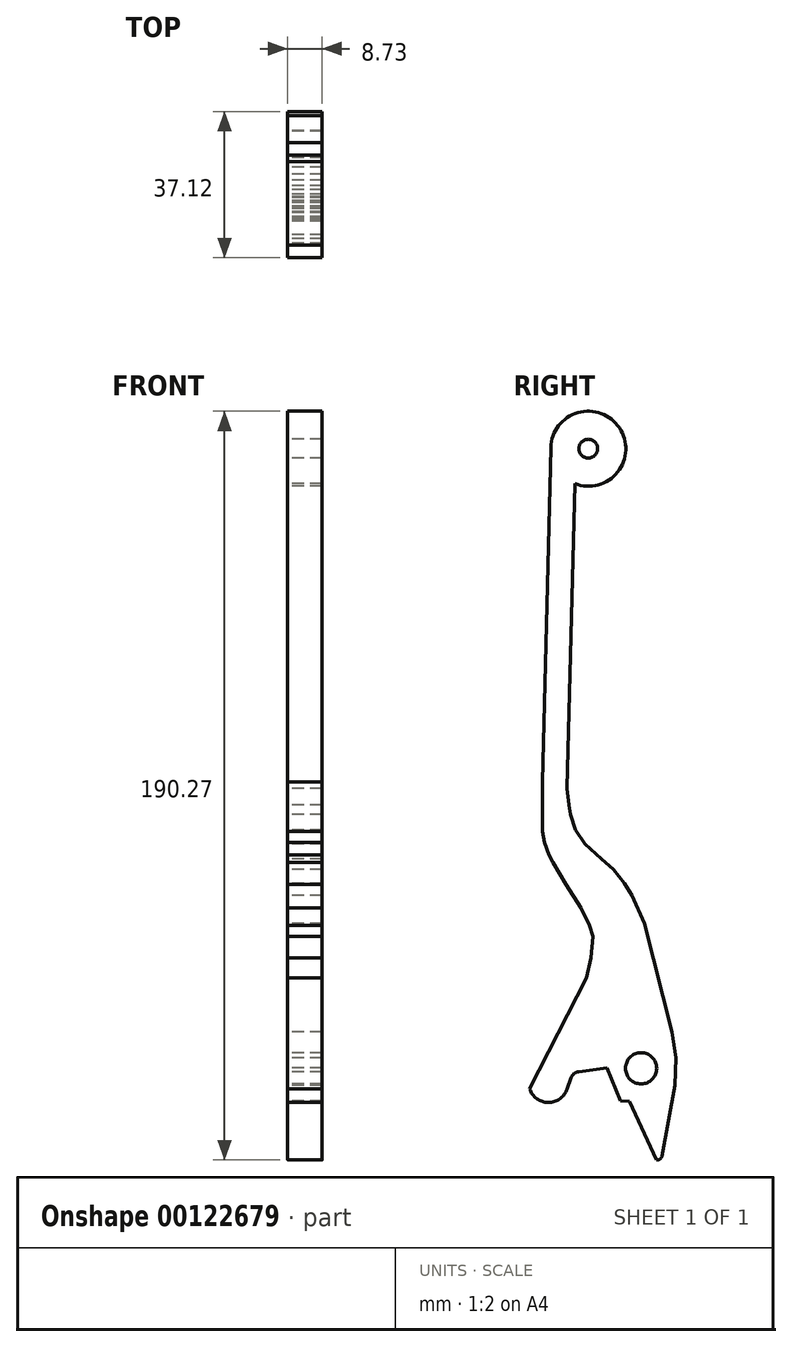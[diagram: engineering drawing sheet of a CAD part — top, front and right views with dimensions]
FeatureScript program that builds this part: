
annotation { "Feature Type Name" : "Feature", "Feature Type Description" : "" }
export const myFeature = defineFeature(function(context is Context, id is Id, definition is map)
    precondition{}
    {
        {
            var Q0;
            Q0=qCreatedBy(makeId("Right.planeOp"),FACE);
            var sketch = newSketch(context, id + "F0", { "sketchPlane" : qUnion([Q0])});
            skLineSegment(sketch, "E0", {"start": v(18.14, 76.71) * mm, "end": v(13.92, -75.63) * mm});
            skLineSegment(sketch, "E1", {"start": v(-35.24, -55.96) * mm, "end": v(-22.74, -31.58) * mm});
            skLineSegment(sketch, "E2", {"start": v(-22.7, -51.6) * mm, "end": v(-15.56, -50.57) * mm});
            skLineSegment(sketch, "E3", {"start": v(-12.21, -58.94) * mm, "end": v(-9.84, -59.08) * mm});
            skLineSegment(sketch, "E4", {"start": v(-9.84, -59.08) * mm, "end": v(-3.05, -74) * mm});
            skLineSegment(sketch, "E5", {"start": v(-1.7, -73.13) * mm, "end": v(1.67, -55.09) * mm});
            skLineSegment(sketch, "E6", {"start": v(1.67, -55.09) * mm, "end": v(1.88, -48.09) * mm});
            skLineSegment(sketch, "E7", {"start": v(1.88, -48.09) * mm, "end": v(0.85, -41.52) * mm});
            skLineSegment(sketch, "E8", {"start": v(0.85, -41.52) * mm, "end": v(-6.04, -13.87) * mm});
            skLineSegment(sketch, "E9", {"start": v(-6.04, -13.87) * mm, "end": v(-9.21, -6.82) * mm});
            skLineSegment(sketch, "E10", {"start": v(-9.21, -6.82) * mm, "end": v(-11.14, -3.78) * mm});
            skLineSegment(sketch, "E11", {"start": v(-11.14, -3.78) * mm, "end": v(-14.02, -0.25) * mm});
            skLineSegment(sketch, "E12", {"start": v(-14.02, -0.25) * mm, "end": v(-16.96, 2.48) * mm});
            skLineSegment(sketch, "E13", {"start": v(-16.96, 2.48) * mm, "end": v(-21.24, 6.3) * mm});
            skLineSegment(sketch, "E14", {"start": v(-21.24, 6.3) * mm, "end": v(-23.6, 9.79) * mm});
            skLineSegment(sketch, "E15", {"start": v(-23.6, 9.79) * mm, "end": v(-24.84, 13.8) * mm});
            skLineSegment(sketch, "E16", {"start": v(-12.21, -58.94) * mm, "end": v(-15.56, -50.57) * mm});
            skArc(sketch, "E17", {"start": v(-3.05, -74) * mm, "mid": v(-2.18, -73.85) * mm, "end": v(-1.7, -73.13) * mm});
            skCircle(sketch, "E18", {"center": v(-6.92, -50.72) * mm, "radius": 3.97 * mm});
            skPoint(sketch, "E18.first.point", {"position": v(-10.87, -50.32) * mm});
            skPoint(sketch, "E18.second.point", {"position": v(-4.6, -47.5) * mm});
            skPoint(sketch, "E18.third.point", {"position": v(-4.98, -54.18) * mm});
            skLineSegment(sketch, "E19", {"start": v(-22.74, -31.58) * mm, "end": v(-20.76, -27.73) * mm});
            skLineSegment(sketch, "E20", {"start": v(-20.76, -27.73) * mm, "end": v(-19.68, -22.73) * mm});
            skLineSegment(sketch, "E21", {"start": v(-19.68, -22.73) * mm, "end": v(-19.12, -17.24) * mm});
            skLineSegment(sketch, "E22", {"start": v(-19.12, -17.24) * mm, "end": v(-20.01, -14.48) * mm});
            skLineSegment(sketch, "E23", {"start": v(-20.01, -14.48) * mm, "end": v(-22.19, -10.01) * mm});
            skLineSegment(sketch, "E24", {"start": v(-22.19, -10.01) * mm, "end": v(-26, -3.94) * mm});
            skLineSegment(sketch, "E25", {"start": v(-26, -3.94) * mm, "end": v(-29.34, 1.54) * mm});
            skLineSegment(sketch, "E26", {"start": v(-29.34, 1.54) * mm, "end": v(-30.36, 3.5) * mm});
            skLineSegment(sketch, "E27", {"start": v(-30.36, 3.5) * mm, "end": v(-31.48, 6.64) * mm});
            skLineSegment(sketch, "E28", {"start": v(-31.48, 6.64) * mm, "end": v(-32.03, 9.45) * mm});
            skLineSegment(sketch, "E29", {"start": v(-32.03, 9.45) * mm, "end": v(-32.03, 12.06) * mm});
            skLineSegment(sketch, "E30", {"start": v(-32.03, 12.06) * mm, "end": v(-32.03, 22.09) * mm});
            skLineSegment(sketch, "E31", {"start": v(-24.84, 13.8) * mm, "end": v(-25.28, 16.24) * mm});
            skLineSegment(sketch, "E32", {"start": v(-25.28, 16.24) * mm, "end": v(-25.72, 20.38) * mm});
            skLineSegment(sketch, "E33", {"start": v(-32.03, 22.09) * mm, "end": v(-29.86, 107.09) * mm});
            skArc(sketch, "E34", {"start": v(-23.75, 97.82) * mm, "mid": v(-12.43, 112.01) * mm, "end": v(-29.86, 106.96) * mm});
            skLineSegment(sketch, "E35", {"start": v(-25.72, 20.38) * mm, "end": v(-23.75, 97.82) * mm});
            skCircle(sketch, "E36", {"center": v(-20.34, 106.71) * mm, "radius": 2.38 * mm});
            skLineSegment(sketch, "E37", {"start": v(-24.7, -53.1) * mm, "end": v(-25.72, -56.03) * mm});
            skArc(sketch, "E38", {"start": v(-22.7, -51.6) * mm, "mid": v(-23.93, -52.04) * mm, "end": v(-24.7, -53.1) * mm});
            skArc(sketch, "E39", {"start": v(-35.24, -55.96) * mm, "mid": v(-30.5, -59.4) * mm, "end": v(-25.72, -56.03) * mm});
            skSolve(sketch);
        }
        {
            var Q0;
            Q0=makeQuery(id+"F0.imprint","IMPRINT",FACE,{"disambiguationData":[TD([[makeQuery(id+"F0.imprint","IMPRINT",EDGE,{"derivedFrom":sQuery(id+"F0.wireOp",EDGE,"E1")}),-1.0]])]});
            extrude(context, id + "F1", {"entities" : qUnion([Q0]), "depth" : 8.73 * mm});
        }
    });
